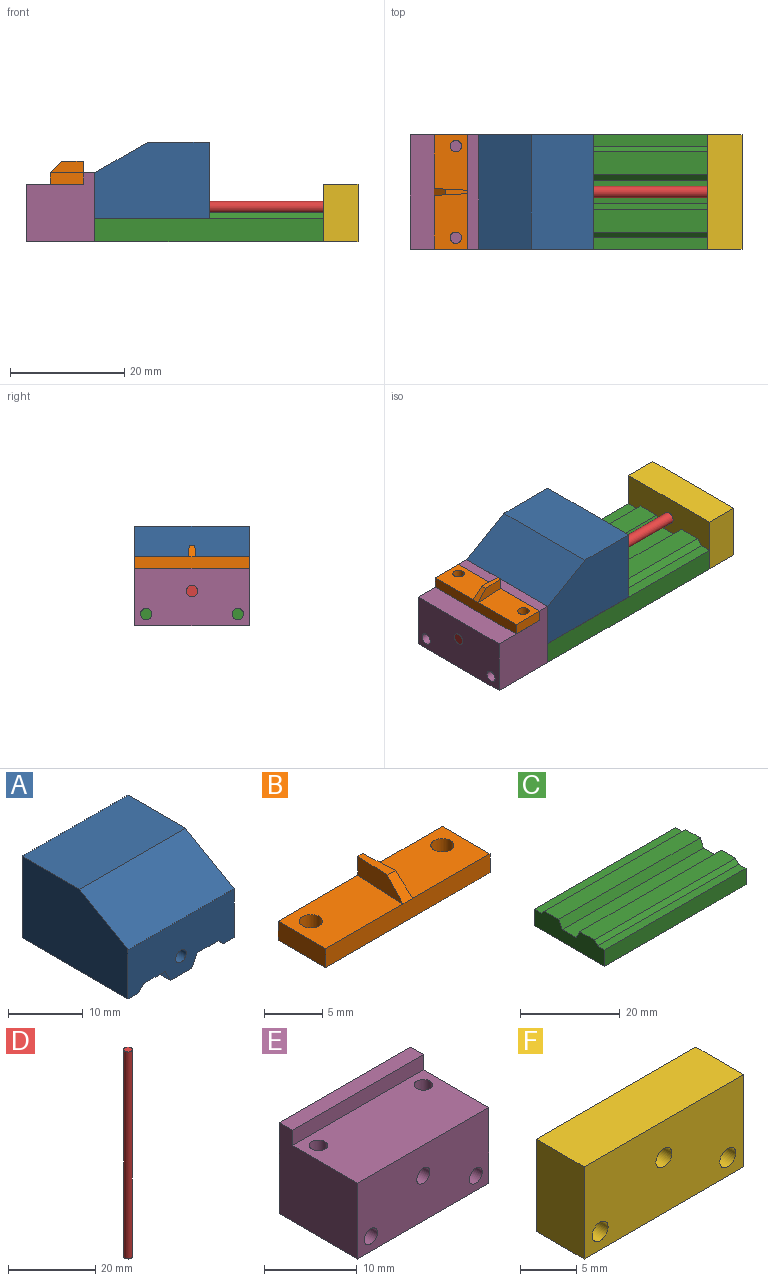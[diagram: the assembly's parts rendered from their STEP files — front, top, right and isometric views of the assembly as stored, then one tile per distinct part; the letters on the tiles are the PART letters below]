
ASSEMBLY  parts=6 mates=5
PART A: 16 faces, bbox 20x20x14.3 mm
  f0: plane 20x4mm, normal (0,0,-1), area 80mm2, adj f1,f2,f7,f11
  f1: plane 20x14.3mm, normal (0,1,0), area 257.9mm2, adj f0,f3,f4,f5,f6,f7,f8,f9
  f2: plane 20x9mm, normal (0,-1,0), area 151.9mm2, adj f0,f3,f4,f5,f6,f7,f8,f9
  f3: plane 20x13.3mm, normal (1,0,0), area 241.7mm2, adj f1,f2,f6,f14,f15
  f4: plane 20x13.3mm, normal (-1,0,0), area 241.7mm2, adj f1,f2,f10,f14,f15
  f5: cylinder r=1mm len=20mm, axis (0,-1,0), area 125.7mm2, adj f1,f2
  f6: plane 20x2mm, normal (0,0,-1), area 40mm2, adj f1,f2,f3,f8
  f7: plane 20x2mm, normal (0.89,0,-0.45), area 44.7mm2, adj f0,f1,f2,f9
  f8: plane 20x1mm, normal (-0.71,0,-0.71), area 28.3mm2, adj f1,f2,f6,f9
  f9: plane 20x4mm, normal (0,0,-1), area 80mm2, adj f1,f2,f7,f8
  f10: plane 20x2mm, normal (0,0,-1), area 40mm2, adj f1,f2,f4,f12
  f11: plane 20x2mm, normal (-0.89,0,-0.45), area 44.7mm2, adj f0,f1,f2,f13
  f12: plane 20x1mm, normal (0.71,0,-0.71), area 28.3mm2, adj f1,f2,f10,f13
  f13: plane 20x4mm, normal (0,0,-1), area 80mm2, adj f1,f2,f11,f12
  f14: plane 20x9.18mm, normal (0,-0.5,0.87), area 212mm2, adj f2,f3,f4,f15
  f15: plane 20x10.82mm, normal (0,0,1), area 216.4mm2, adj f1,f3,f4,f14
PART B: 13 faces, bbox 20x5.8x4 mm
  f0: plane 9.7x5.8mm, normal (0,0,1), area 52.2mm2, adj f2,f3,f4,f5,f10
  f1: plane 5.8x2mm, normal (1,0,0), area 11.6mm2, adj f2,f5,f7,f8
  f2: plane 20x4mm, normal (0,1,0), area 41.2mm2, adj f0,f1,f3,f7,f8,f9,f10,f11
  f3: plane 5.8x2mm, normal (-1,0,0), area 11.6mm2, adj f0,f2,f5,f8
  f4: cylinder r=1mm len=2mm, axis (0,0,-1), area 12.6mm2, adj f0,f8
  f5: plane 20x2mm, normal (0,-1,0), area 40mm2, adj f0,f1,f3,f7,f8,f12
  f6: cylinder r=1mm len=2mm, axis (0,0,-1), area 12.6mm2, adj f7,f8
  f7: plane 9.7x5.8mm, normal (0,0,1), area 52.2mm2, adj f1,f2,f5,f6,f9
  f8: plane 20x5.8mm, normal (0,0,-1), area 109.7mm2, adj f1,f2,f3,f4,f5,f6
  f9: plane 5.8x2mm, normal (1,0.05,0), area 9.6mm2, adj f2,f7,f11,f12
  f10: plane 5.8x2mm, normal (-1,0.05,0), area 9.6mm2, adj f0,f2,f11,f12
  f11: plane 3.8x0.99mm, normal (0,0,1), area 3mm2, adj f2,f9,f10,f12
  f12: plane 2x2mm, normal (0,-0.71,0.71), area 3.1mm2, adj f5,f9,f10,f11
PART C: 14 faces, bbox 40x20x5 mm
  f0: plane 40x4mm, normal (0,0,1), area 160mm2, adj f2,f3,f9,f12
  f1: plane 40x4mm, normal (0,0,1), area 160mm2, adj f2,f3,f7,f11
  f2: plane 20x5mm, normal (1,0,0), area 85mm2, adj f0,f1,f4,f5,f6,f7,f8,f9
  f3: plane 20x5mm, normal (-1,0,0), area 85mm2, adj f0,f1,f4,f5,f6,f7,f8,f9
  f4: plane 40x4mm, normal (0,1,0), area 160mm2, adj f2,f3,f6,f8
  f5: plane 40x4mm, normal (0,-1,0), area 160mm2, adj f2,f3,f6,f13
  f6: plane 40x20mm, normal (0,0,-1), area 800mm2, adj f2,f3,f4,f5
  f7: plane 40x1mm, normal (0,0.71,0.71), area 56.6mm2, adj f1,f2,f3,f8
  f8: plane 40x2mm, normal (0,0,1), area 80mm2, adj f2,f3,f4,f7
  f9: plane 40x2mm, normal (0,0.89,0.45), area 89.4mm2, adj f0,f2,f3,f10
  f10: plane 40x4mm, normal (0,0,1), area 160mm2, adj f2,f3,f9,f11
  f11: plane 40x2mm, normal (0,-0.89,0.45), area 89.4mm2, adj f1,f2,f3,f10
  f12: plane 40x1mm, normal (0,-0.71,0.71), area 56.6mm2, adj f0,f2,f3,f13
  f13: plane 40x2mm, normal (0,0,1), area 80mm2, adj f2,f3,f5,f12
PART D: 3 faces, bbox 2x2x58 mm
  f0: cylinder r=1mm len=58mm, axis (0,0,-1), area 364.4mm2, adj f1,f2
  f1: plane 2x2mm, normal (0,0,1), area 3.1mm2, adj f0
  f2: plane 2x2mm, normal (0,0,-1), area 3.1mm2, adj f0
PART E: 15 faces, bbox 20x12x12 mm
  f0: plane 20x10mm, normal (0,0,1), area 193.7mm2, adj f1,f3,f4,f6,f11,f13
  f1: plane 12x12mm, normal (1,0,0), area 124mm2, adj f0,f2,f4,f5,f6,f7
  f2: plane 20x12mm, normal (0,1,0), area 230.6mm2, adj f1,f3,f5,f7,f8,f9,f10
  f3: plane 12x12mm, normal (-1,0,0), area 124mm2, adj f0,f2,f4,f5,f6,f7
  f4: plane 20x10mm, normal (0,-1,0), area 190.6mm2, adj f0,f1,f3,f5,f8,f9,f10
  f5: plane 20x12mm, normal (0,0,-1), area 240mm2, adj f1,f2,f3,f4
  f6: plane 20x2mm, normal (0,-1,0), area 40mm2, adj f0,f1,f3,f7
  f7: plane 20x2mm, normal (0,0,1), area 40mm2, adj f1,f2,f3,f6
  f8: cylinder r=1mm len=12mm, axis (0,-1,0), area 75.4mm2, adj f2,f4
  f9: cylinder r=1mm len=12mm, axis (0,-1,0), area 75.4mm2, adj f2,f4
  f10: cylinder r=1mm len=12mm, axis (0,-1,0), area 75.4mm2, adj f2,f4
  f11: cylinder r=1mm len=4mm, axis (0,0,1), area 25.1mm2, adj f0,f12
  f12: plane 2x2mm, normal (0,0,1), area 3.1mm2, adj f11
  f13: cylinder r=1mm len=4mm, axis (0,0,1), area 25.1mm2, adj f0,f14
  f14: plane 2x2mm, normal (0,0,1), area 3.1mm2, adj f13
PART F: 9 faces, bbox 20x6x10 mm
  f0: plane 20x6mm, normal (0,0,-1), area 120mm2, adj f1,f4,f7,f8
  f1: plane 10x6mm, normal (1,0,0), area 60mm2, adj f0,f2,f7,f8
  f2: plane 20x6mm, normal (0,0,1), area 120mm2, adj f1,f4,f7,f8
  f3: cylinder r=1mm len=6mm, axis (0,1,0), area 37.7mm2, adj f7,f8
  f4: plane 10x6mm, normal (-1,0,0), area 60mm2, adj f0,f2,f7,f8
  f5: cylinder r=1mm len=6mm, axis (0,1,0), area 37.7mm2, adj f7,f8
  f6: cylinder r=1mm len=6mm, axis (0,1,0), area 37.7mm2, adj f7,f8
  f7: plane 20x10mm, normal (0,-1,0), area 190.6mm2, adj f0,f1,f2,f3,f4,f5,f6
  f8: plane 20x10mm, normal (0,1,0), area 190.6mm2, adj f0,f1,f2,f3,f4,f5,f6
PLACE A rot(axis=(0,0,-1),90deg) t=(-11.82,-5.27,5.72)mm
PLACE B rot(axis=(0,0,-1),90deg) t=(-26.73,-5.27,12.72)mm
PLACE C t=(-1.83,-5.27,2.72)mm
PLACE D rot(axis=(0,1,0),90deg) t=(-33.83,-5.27,8.72)mm
PLACE E rot(axis=(0,0,-1),90deg) t=(-27.83,-5.27,2.72)mm
PLACE F rot(axis=(0,0,-1),90deg) t=(24.17,-5.27,7.72)mm
MATE fastened E.f2 <-> C.f3  axis (1,0,0) through (-21.83,-15.27,2.72)mm
MATE fastened B.f8 <-> E.f0  axis (0,0,-1) through (-23.83,-15.27,12.72)mm
MATE fastened D.f0 <-> F.f5  axis (1,0,0) through (24.17,-5.27,8.72)mm
MATE fastened F.f7 <-> C.f2  axis (-1,0,0) through (18.17,4.73,2.72)mm
MATE slider A.f5 <-> D.f0  axis (-1,0,0) through (-11.82,-5.27,8.72)mm
